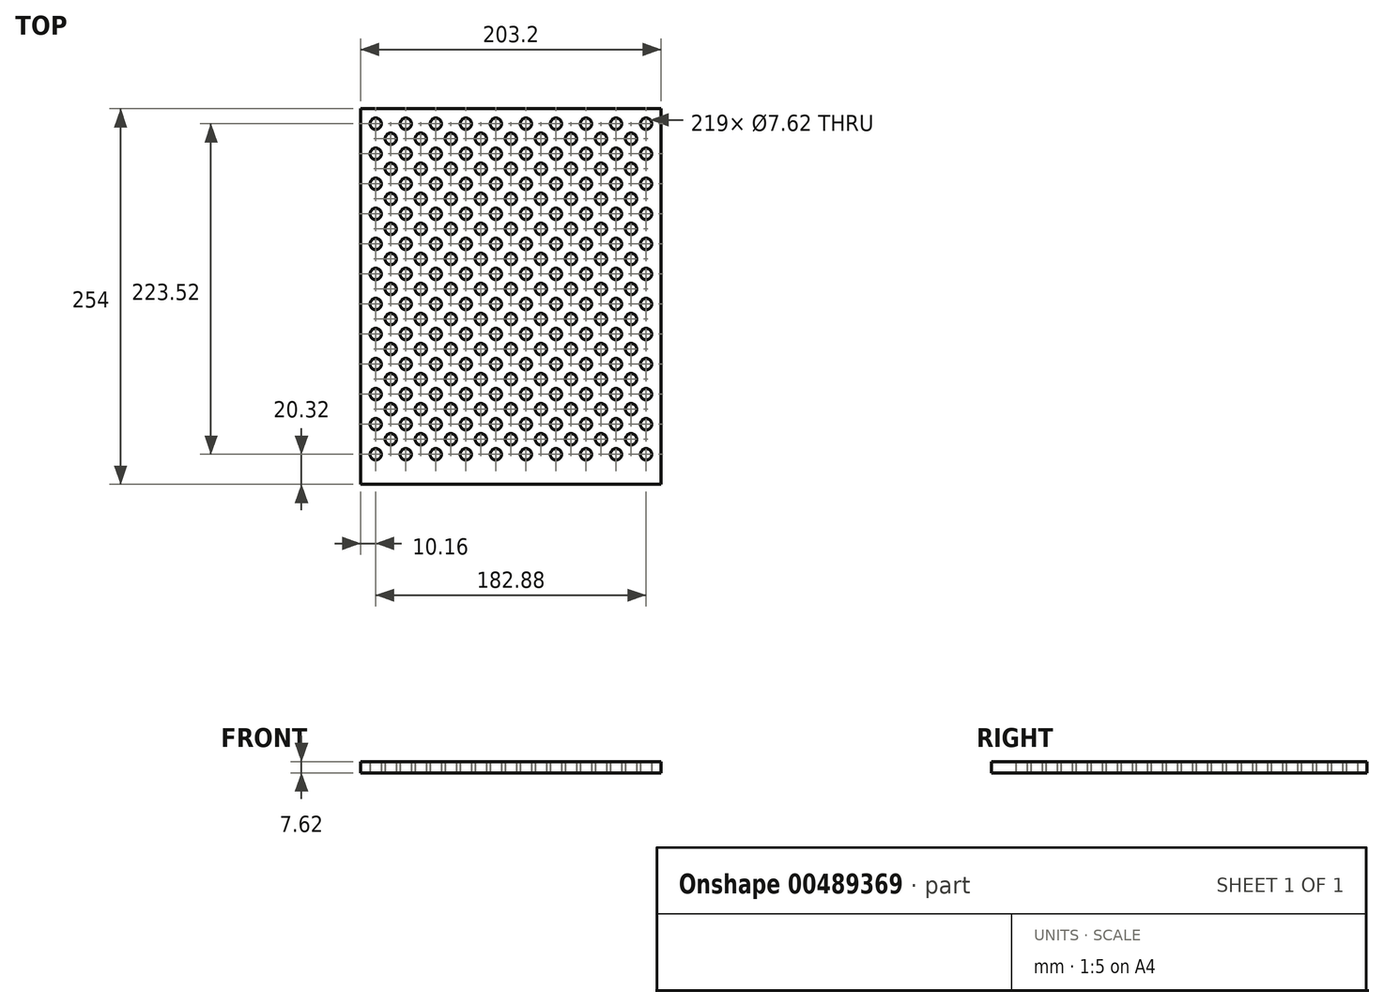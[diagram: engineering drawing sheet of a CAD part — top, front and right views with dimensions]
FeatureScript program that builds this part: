
annotation { "Feature Type Name" : "Feature", "Feature Type Description" : "" }
export const myFeature = defineFeature(function(context is Context, id is Id, definition is map)
    precondition{}
    {
        {
            var Q0;
            Q0=qCreatedBy(makeId("Top.planeOp"),FACE);
            var sketch = newSketch(context, id + "F0", { "sketchPlane" : qUnion([Q0])});
            skLineSegment(sketch, "E0.bottom", {"start": v(-101.6, 127) * mm, "end": v(101.6, 127) * mm});
            skLineSegment(sketch, "E0.top", {"start": v(-101.6, -127) * mm, "end": v(101.6, -127) * mm});
            skLineSegment(sketch, "E0.left", {"start": v(-101.6, 127) * mm, "end": v(-101.6, -127) * mm});
            skLineSegment(sketch, "E0.right", {"start": v(101.6, 127) * mm, "end": v(101.6, -127) * mm});
            skCircle(sketch, "E1", {"center": v(-91.44, 116.84) * mm, "radius": 3.8 * mm});
            skCircle(sketch, "E2", {"center": v(-81.28, 106.68) * mm, "radius": 3.8 * mm});
            skCircle(sketch, "E3", {"center": v(-91.44, 96.52) * mm, "radius": 3.8 * mm});
            skCircle(sketch, "E4", {"center": v(-81.28, 66.04) * mm, "radius": 3.8 * mm});
            skCircle(sketch, "E5", {"center": v(-91.44, 76.2) * mm, "radius": 3.8 * mm});
            skCircle(sketch, "E6", {"center": v(-81.28, 86.36) * mm, "radius": 3.8 * mm});
            skCircle(sketch, "E7", {"center": v(-91.44, 55.88) * mm, "radius": 3.8 * mm});
            skCircle(sketch, "E8", {"center": v(-81.28, 45.72) * mm, "radius": 3.8 * mm});
            skCircle(sketch, "E9", {"center": v(-91.44, 35.56) * mm, "radius": 3.8 * mm});
            skCircle(sketch, "E10", {"center": v(-81.28, 25.4) * mm, "radius": 3.8 * mm});
            skCircle(sketch, "E11", {"center": v(-91.44, 15.24) * mm, "radius": 3.8 * mm});
            skCircle(sketch, "E12", {"center": v(-91.44, -5.08) * mm, "radius": 3.8 * mm});
            skCircle(sketch, "E13", {"center": v(-81.28, 5.08) * mm, "radius": 3.8 * mm});
            skCircle(sketch, "E14", {"center": v(-81.28, -15.24) * mm, "radius": 3.8 * mm});
            skCircle(sketch, "E15", {"center": v(-91.44, -25.4) * mm, "radius": 3.8 * mm});
            skCircle(sketch, "E16", {"center": v(-81.28, -35.56) * mm, "radius": 3.8 * mm});
            skCircle(sketch, "E17", {"center": v(-91.44, -86.36) * mm, "radius": 3.8 * mm});
            skCircle(sketch, "E18", {"center": v(-91.44, -45.72) * mm, "radius": 3.8 * mm});
            skCircle(sketch, "E19", {"center": v(-81.28, -76.2) * mm, "radius": 3.8 * mm});
            skCircle(sketch, "E20", {"center": v(-81.28, -55.88) * mm, "radius": 3.8 * mm});
            skCircle(sketch, "E21", {"center": v(-81.28, -96.52) * mm, "radius": 3.8 * mm});
            skCircle(sketch, "E22", {"center": v(-91.44, -66.04) * mm, "radius": 3.8 * mm});
            skCircle(sketch, "E23", {"center": v(-91.44, -106.68) * mm, "radius": 3.8 * mm});
            skLineSegment(sketch, "E24", {"start": v(-91.44, 116.84) * mm, "end": v(-91.44, -106.68) * mm});
            skLineSegment(sketch, "E25", {"start": v(-81.28, 127) * mm, "end": v(-81.28, -127) * mm, "construction": true});
            skCircle(sketch, "E26.MirrorC", {"center": v(-71.12, 116.84) * mm, "radius": 3.8 * mm});
            skCircle(sketch, "E27.MirrorC", {"center": v(-71.12, 96.52) * mm, "radius": 3.8 * mm});
            skCircle(sketch, "E28.MirrorC", {"center": v(-71.12, 76.2) * mm, "radius": 3.8 * mm});
            skCircle(sketch, "E29.MirrorC", {"center": v(-71.12, 55.88) * mm, "radius": 3.8 * mm});
            skCircle(sketch, "E30.MirrorC", {"center": v(-71.12, 35.56) * mm, "radius": 3.8 * mm});
            skCircle(sketch, "E31.MirrorC", {"center": v(-71.12, 15.24) * mm, "radius": 3.8 * mm});
            skCircle(sketch, "E32.MirrorC", {"center": v(-71.12, -5.08) * mm, "radius": 3.8 * mm});
            skCircle(sketch, "E33.MirrorC", {"center": v(-71.12, -25.4) * mm, "radius": 3.8 * mm});
            skCircle(sketch, "E34.MirrorC", {"center": v(-71.12, -45.72) * mm, "radius": 3.8 * mm});
            skCircle(sketch, "E35.MirrorC", {"center": v(-71.12, -66.04) * mm, "radius": 3.8 * mm});
            skCircle(sketch, "E36.MirrorC", {"center": v(-71.12, -86.36) * mm, "radius": 3.8 * mm});
            skCircle(sketch, "E37.MirrorC", {"center": v(-71.12, -106.68) * mm, "radius": 3.8 * mm});
            skLineSegment(sketch, "E38", {"start": v(-71.12, 127) * mm, "end": v(-71.12, -127) * mm, "construction": true});
            skCircle(sketch, "E39.MirrorC", {"center": v(-60.96, 106.68) * mm, "radius": 3.8 * mm});
            skCircle(sketch, "E40.MirrorC", {"center": v(-60.96, 86.36) * mm, "radius": 3.8 * mm});
            skCircle(sketch, "E41.MirrorC", {"center": v(-60.96, 66.04) * mm, "radius": 3.8 * mm});
            skCircle(sketch, "E42.MirrorC", {"center": v(-60.96, 45.72) * mm, "radius": 3.8 * mm});
            skCircle(sketch, "E43.MirrorC", {"center": v(-60.96, 25.4) * mm, "radius": 3.8 * mm});
            skCircle(sketch, "E44.MirrorC", {"center": v(-60.96, 5.08) * mm, "radius": 3.8 * mm});
            skCircle(sketch, "E45.MirrorC", {"center": v(-60.96, -15.24) * mm, "radius": 3.8 * mm});
            skCircle(sketch, "E46.MirrorC", {"center": v(-60.96, -35.56) * mm, "radius": 3.8 * mm});
            skCircle(sketch, "E47.MirrorC", {"center": v(-60.96, -55.88) * mm, "radius": 3.8 * mm});
            skCircle(sketch, "E48.MirrorC", {"center": v(-60.96, -76.2) * mm, "radius": 3.8 * mm});
            skCircle(sketch, "E49.MirrorC", {"center": v(-60.96, -96.52) * mm, "radius": 3.8 * mm});
            skLineSegment(sketch, "E50", {"start": v(-60.96, 127) * mm, "end": v(-60.96, -127) * mm, "construction": true});
            skCircle(sketch, "E51.MirrorC", {"center": v(-50.8, 116.84) * mm, "radius": 3.8 * mm});
            skCircle(sketch, "E52.MirrorC", {"center": v(-50.8, 96.52) * mm, "radius": 3.8 * mm});
            skCircle(sketch, "E53.MirrorC", {"center": v(-50.8, 76.2) * mm, "radius": 3.8 * mm});
            skCircle(sketch, "E54.MirrorC", {"center": v(-50.8, 55.88) * mm, "radius": 3.8 * mm});
            skCircle(sketch, "E55.MirrorC", {"center": v(-50.8, 35.56) * mm, "radius": 3.8 * mm});
            skCircle(sketch, "E56.MirrorC", {"center": v(-50.8, 15.24) * mm, "radius": 3.8 * mm});
            skCircle(sketch, "E57.MirrorC", {"center": v(-50.8, -5.08) * mm, "radius": 3.8 * mm});
            skCircle(sketch, "E58.MirrorC", {"center": v(-50.8, -25.4) * mm, "radius": 3.8 * mm});
            skCircle(sketch, "E59.MirrorC", {"center": v(-50.8, -45.72) * mm, "radius": 3.8 * mm});
            skCircle(sketch, "E60.MirrorC", {"center": v(-50.8, -66.04) * mm, "radius": 3.8 * mm});
            skCircle(sketch, "E61.MirrorC", {"center": v(-50.8, -86.36) * mm, "radius": 3.8 * mm});
            skCircle(sketch, "E62.MirrorC", {"center": v(-50.8, -106.68) * mm, "radius": 3.8 * mm});
            skLineSegment(sketch, "E63", {"start": v(-50.8, 127) * mm, "end": v(-50.8, -127) * mm, "construction": true});
            skCircle(sketch, "E64.MirrorC", {"center": v(-40.64, -96.52) * mm, "radius": 3.8 * mm});
            skCircle(sketch, "E65.MirrorC", {"center": v(-40.64, -76.2) * mm, "radius": 3.8 * mm});
            skCircle(sketch, "E66.MirrorC", {"center": v(-40.64, -55.88) * mm, "radius": 3.8 * mm});
            skCircle(sketch, "E67.MirrorC", {"center": v(-40.64, -35.56) * mm, "radius": 3.8 * mm});
            skCircle(sketch, "E68.MirrorC", {"center": v(-40.64, 5.08) * mm, "radius": 3.8 * mm});
            skCircle(sketch, "E69.MirrorC", {"center": v(-40.64, 25.4) * mm, "radius": 3.8 * mm});
            skCircle(sketch, "E70.MirrorC", {"center": v(-40.64, 45.72) * mm, "radius": 3.8 * mm});
            skCircle(sketch, "E71.MirrorC", {"center": v(-40.64, 66.04) * mm, "radius": 3.8 * mm});
            skCircle(sketch, "E72.MirrorC", {"center": v(-40.64, 86.36) * mm, "radius": 3.8 * mm});
            skCircle(sketch, "E73.MirrorC", {"center": v(-40.64, 106.68) * mm, "radius": 3.8 * mm});
            skCircle(sketch, "E74.MirrorC", {"center": v(-40.64, -15.24) * mm, "radius": 3.8 * mm});
            skLineSegment(sketch, "E75", {"start": v(-40.64, 127) * mm, "end": v(-40.64, -127) * mm, "construction": true});
            skCircle(sketch, "E76.MirrorC", {"center": v(-30.48, 116.84) * mm, "radius": 3.8 * mm});
            skCircle(sketch, "E77.MirrorC", {"center": v(-30.48, 96.52) * mm, "radius": 3.8 * mm});
            skCircle(sketch, "E78.MirrorC", {"center": v(-30.48, 76.2) * mm, "radius": 3.8 * mm});
            skCircle(sketch, "E79.MirrorC", {"center": v(-30.48, 55.88) * mm, "radius": 3.8 * mm});
            skCircle(sketch, "E80.MirrorC", {"center": v(-30.48, 35.56) * mm, "radius": 3.8 * mm});
            skCircle(sketch, "E81.MirrorC", {"center": v(-30.48, 15.24) * mm, "radius": 3.8 * mm});
            skCircle(sketch, "E82.MirrorC", {"center": v(-30.48, -5.08) * mm, "radius": 3.8 * mm});
            skCircle(sketch, "E83.MirrorC", {"center": v(-30.48, -25.4) * mm, "radius": 3.8 * mm});
            skCircle(sketch, "E84.MirrorC", {"center": v(-30.48, -45.72) * mm, "radius": 3.8 * mm});
            skCircle(sketch, "E85.MirrorC", {"center": v(-30.48, -66.04) * mm, "radius": 3.8 * mm});
            skCircle(sketch, "E86.MirrorC", {"center": v(-30.48, -86.36) * mm, "radius": 3.8 * mm});
            skCircle(sketch, "E87.MirrorC", {"center": v(-30.48, -106.68) * mm, "radius": 3.8 * mm});
            skLineSegment(sketch, "E88", {"start": v(-30.48, 127) * mm, "end": v(-30.48, -127) * mm, "construction": true});
            skCircle(sketch, "E89.MirrorC", {"center": v(-20.32, 106.68) * mm, "radius": 3.8 * mm});
            skCircle(sketch, "E90.MirrorC", {"center": v(-20.32, 86.36) * mm, "radius": 3.8 * mm});
            skCircle(sketch, "E91.MirrorC", {"center": v(-20.32, 45.72) * mm, "radius": 3.8 * mm});
            skCircle(sketch, "E92.MirrorC", {"center": v(-20.32, 5.08) * mm, "radius": 3.8 * mm});
            skCircle(sketch, "E93.MirrorC", {"center": v(-20.32, -35.56) * mm, "radius": 3.8 * mm});
            skCircle(sketch, "E94.MirrorC", {"center": v(-20.32, -15.24) * mm, "radius": 3.8 * mm});
            skCircle(sketch, "E95.MirrorC", {"center": v(-20.32, -55.88) * mm, "radius": 3.8 * mm});
            skCircle(sketch, "E96.MirrorC", {"center": v(-20.32, -76.2) * mm, "radius": 3.8 * mm});
            skCircle(sketch, "E97.MirrorC", {"center": v(-20.32, -96.52) * mm, "radius": 3.8 * mm});
            skCircle(sketch, "E98.MirrorC", {"center": v(-20.32, 25.4) * mm, "radius": 3.8 * mm});
            skCircle(sketch, "E99.MirrorC", {"center": v(-20.32, 66.04) * mm, "radius": 3.8 * mm});
            skLineSegment(sketch, "E100", {"start": v(-20.32, 127) * mm, "end": v(-20.32, -127) * mm, "construction": true});
            skCircle(sketch, "E101.MirrorC", {"center": v(-10.16, 116.84) * mm, "radius": 3.8 * mm});
            skCircle(sketch, "E102.MirrorC", {"center": v(-10.16, 96.52) * mm, "radius": 3.8 * mm});
            skCircle(sketch, "E103.MirrorC", {"center": v(-10.16, 76.2) * mm, "radius": 3.8 * mm});
            skCircle(sketch, "E104.MirrorC", {"center": v(-10.16, 55.88) * mm, "radius": 3.8 * mm});
            skCircle(sketch, "E105.MirrorC", {"center": v(-10.16, 35.56) * mm, "radius": 3.8 * mm});
            skCircle(sketch, "E106.MirrorC", {"center": v(-10.16, 15.24) * mm, "radius": 3.8 * mm});
            skCircle(sketch, "E107.MirrorC", {"center": v(-10.16, -5.08) * mm, "radius": 3.8 * mm});
            skCircle(sketch, "E108.MirrorC", {"center": v(-10.16, -25.4) * mm, "radius": 3.8 * mm});
            skCircle(sketch, "E109.MirrorC", {"center": v(-10.16, -45.72) * mm, "radius": 3.8 * mm});
            skCircle(sketch, "E110.MirrorC", {"center": v(-10.16, -66.04) * mm, "radius": 3.8 * mm});
            skCircle(sketch, "E111.MirrorC", {"center": v(-10.16, -86.36) * mm, "radius": 3.8 * mm});
            skCircle(sketch, "E112.MirrorC", {"center": v(-10.16, -106.68) * mm, "radius": 3.8 * mm});
            skLineSegment(sketch, "E113", {"start": v(-10.16, -127) * mm, "end": v(-10.16, 127) * mm, "construction": true});
            skCircle(sketch, "E114.MirrorC", {"center": v(0, 106.68) * mm, "radius": 3.8 * mm});
            skCircle(sketch, "E115.MirrorC", {"center": v(0, 86.36) * mm, "radius": 3.8 * mm});
            skCircle(sketch, "E116.MirrorC", {"center": v(0, 66.04) * mm, "radius": 3.8 * mm});
            skCircle(sketch, "E117.MirrorC", {"center": v(0, 45.72) * mm, "radius": 3.8 * mm});
            skCircle(sketch, "E118.MirrorC", {"center": v(0, 25.4) * mm, "radius": 3.8 * mm});
            skCircle(sketch, "E119.MirrorC", {"center": v(0, 5.08) * mm, "radius": 3.8 * mm});
            skCircle(sketch, "E120.MirrorC", {"center": v(0, -15.24) * mm, "radius": 3.8 * mm});
            skCircle(sketch, "E121.MirrorC", {"center": v(0, -35.56) * mm, "radius": 3.8 * mm});
            skCircle(sketch, "E122.MirrorC", {"center": v(0, -55.88) * mm, "radius": 3.8 * mm});
            skCircle(sketch, "E123.MirrorC", {"center": v(0, -76.2) * mm, "radius": 3.8 * mm});
            skCircle(sketch, "E124.MirrorC", {"center": v(0, -96.52) * mm, "radius": 3.8 * mm});
            skLineSegment(sketch, "E125", {"start": v(0, 127) * mm, "end": v(0, -127) * mm, "construction": true});
            skCircle(sketch, "E126.MirrorC", {"center": v(10.16, -106.68) * mm, "radius": 3.8 * mm});
            skCircle(sketch, "E127.MirrorC", {"center": v(30.48, -106.68) * mm, "radius": 3.8 * mm});
            skCircle(sketch, "E128.MirrorC", {"center": v(50.8, -106.68) * mm, "radius": 3.8 * mm});
            skCircle(sketch, "E129.MirrorC", {"center": v(71.12, -106.68) * mm, "radius": 3.8 * mm});
            skCircle(sketch, "E130.MirrorC", {"center": v(91.44, -106.68) * mm, "radius": 3.8 * mm});
            skCircle(sketch, "E131.MirrorC", {"center": v(81.28, -96.52) * mm, "radius": 3.8 * mm});
            skCircle(sketch, "E132.MirrorC", {"center": v(60.96, -96.52) * mm, "radius": 3.8 * mm});
            skCircle(sketch, "E133.MirrorC", {"center": v(40.64, -96.52) * mm, "radius": 3.8 * mm});
            skCircle(sketch, "E134.MirrorC", {"center": v(20.32, -96.52) * mm, "radius": 3.8 * mm});
            skCircle(sketch, "E135.MirrorC", {"center": v(10.16, -86.36) * mm, "radius": 3.8 * mm});
            skCircle(sketch, "E136.MirrorC", {"center": v(30.48, -86.36) * mm, "radius": 3.8 * mm});
            skCircle(sketch, "E137.MirrorC", {"center": v(50.8, -86.36) * mm, "radius": 3.8 * mm});
            skCircle(sketch, "E138.MirrorC", {"center": v(71.12, -86.36) * mm, "radius": 3.8 * mm});
            skCircle(sketch, "E139.MirrorC", {"center": v(91.44, -86.36) * mm, "radius": 3.8 * mm});
            skCircle(sketch, "E140.MirrorC", {"center": v(81.28, -76.2) * mm, "radius": 3.8 * mm});
            skCircle(sketch, "E141.MirrorC", {"center": v(60.96, -76.2) * mm, "radius": 3.8 * mm});
            skCircle(sketch, "E142.MirrorC", {"center": v(40.64, -76.2) * mm, "radius": 3.8 * mm});
            skCircle(sketch, "E143.MirrorC", {"center": v(20.32, -76.2) * mm, "radius": 3.8 * mm});
            skCircle(sketch, "E144.MirrorC", {"center": v(10.16, -66.04) * mm, "radius": 3.8 * mm});
            skCircle(sketch, "E145.MirrorC", {"center": v(30.48, -66.04) * mm, "radius": 3.8 * mm});
            skCircle(sketch, "E146.MirrorC", {"center": v(50.8, -66.04) * mm, "radius": 3.8 * mm});
            skCircle(sketch, "E147.MirrorC", {"center": v(71.12, -66.04) * mm, "radius": 3.8 * mm});
            skCircle(sketch, "E148.MirrorC", {"center": v(91.44, -66.04) * mm, "radius": 3.8 * mm});
            skCircle(sketch, "E149.MirrorC", {"center": v(81.28, -55.88) * mm, "radius": 3.8 * mm});
            skCircle(sketch, "E150.MirrorC", {"center": v(60.96, -55.88) * mm, "radius": 3.8 * mm});
            skCircle(sketch, "E151.MirrorC", {"center": v(40.64, -55.88) * mm, "radius": 3.8 * mm});
            skCircle(sketch, "E152.MirrorC", {"center": v(20.32, -55.88) * mm, "radius": 3.8 * mm});
            skCircle(sketch, "E153.MirrorC", {"center": v(10.16, -45.72) * mm, "radius": 3.8 * mm});
            skCircle(sketch, "E154.MirrorC", {"center": v(30.48, -45.72) * mm, "radius": 3.8 * mm});
            skCircle(sketch, "E155.MirrorC", {"center": v(50.8, -45.72) * mm, "radius": 3.8 * mm});
            skCircle(sketch, "E156.MirrorC", {"center": v(71.12, -45.72) * mm, "radius": 3.8 * mm});
            skCircle(sketch, "E157.MirrorC", {"center": v(91.44, -45.72) * mm, "radius": 3.8 * mm});
            skCircle(sketch, "E158.MirrorC", {"center": v(81.28, -35.56) * mm, "radius": 3.8 * mm});
            skCircle(sketch, "E159.MirrorC", {"center": v(60.96, -35.56) * mm, "radius": 3.8 * mm});
            skCircle(sketch, "E160.MirrorC", {"center": v(40.64, -35.56) * mm, "radius": 3.8 * mm});
            skCircle(sketch, "E161.MirrorC", {"center": v(20.32, -35.56) * mm, "radius": 3.8 * mm});
            skCircle(sketch, "E162.MirrorC", {"center": v(10.16, -25.4) * mm, "radius": 3.8 * mm});
            skCircle(sketch, "E163.MirrorC", {"center": v(30.48, -25.4) * mm, "radius": 3.8 * mm});
            skCircle(sketch, "E164.MirrorC", {"center": v(50.8, -25.4) * mm, "radius": 3.8 * mm});
            skCircle(sketch, "E165.MirrorC", {"center": v(71.12, -25.4) * mm, "radius": 3.8 * mm});
            skCircle(sketch, "E166.MirrorC", {"center": v(91.44, -25.4) * mm, "radius": 3.8 * mm});
            skCircle(sketch, "E167.MirrorC", {"center": v(20.32, -15.24) * mm, "radius": 3.8 * mm});
            skCircle(sketch, "E168.MirrorC", {"center": v(40.64, -15.24) * mm, "radius": 3.8 * mm});
            skCircle(sketch, "E169.MirrorC", {"center": v(60.96, -15.24) * mm, "radius": 3.8 * mm});
            skCircle(sketch, "E170.MirrorC", {"center": v(81.28, -15.24) * mm, "radius": 3.8 * mm});
            skCircle(sketch, "E171.MirrorC", {"center": v(91.44, -5.08) * mm, "radius": 3.8 * mm});
            skCircle(sketch, "E172.MirrorC", {"center": v(71.12, -5.08) * mm, "radius": 3.8 * mm});
            skCircle(sketch, "E173.MirrorC", {"center": v(50.8, -5.08) * mm, "radius": 3.8 * mm});
            skCircle(sketch, "E174.MirrorC", {"center": v(30.48, -5.08) * mm, "radius": 3.8 * mm});
            skCircle(sketch, "E175.MirrorC", {"center": v(10.16, -5.08) * mm, "radius": 3.8 * mm});
            skCircle(sketch, "E176.MirrorC", {"center": v(20.32, 5.08) * mm, "radius": 3.8 * mm});
            skCircle(sketch, "E177.MirrorC", {"center": v(40.64, 5.08) * mm, "radius": 3.8 * mm});
            skCircle(sketch, "E178.MirrorC", {"center": v(60.96, 5.08) * mm, "radius": 3.8 * mm});
            skCircle(sketch, "E179.MirrorC", {"center": v(81.28, 5.08) * mm, "radius": 3.8 * mm});
            skCircle(sketch, "E180.MirrorC", {"center": v(91.44, 15.24) * mm, "radius": 3.8 * mm});
            skCircle(sketch, "E181.MirrorC", {"center": v(71.12, 15.24) * mm, "radius": 3.8 * mm});
            skCircle(sketch, "E182.MirrorC", {"center": v(50.8, 15.24) * mm, "radius": 3.8 * mm});
            skCircle(sketch, "E183.MirrorC", {"center": v(30.48, 15.24) * mm, "radius": 3.8 * mm});
            skCircle(sketch, "E184.MirrorC", {"center": v(10.16, 15.24) * mm, "radius": 3.8 * mm});
            skCircle(sketch, "E185.MirrorC", {"center": v(20.32, 25.4) * mm, "radius": 3.8 * mm});
            skCircle(sketch, "E186.MirrorC", {"center": v(40.64, 25.4) * mm, "radius": 3.8 * mm});
            skCircle(sketch, "E187.MirrorC", {"center": v(60.96, 25.4) * mm, "radius": 3.8 * mm});
            skCircle(sketch, "E188.MirrorC", {"center": v(81.28, 25.4) * mm, "radius": 3.8 * mm});
            skCircle(sketch, "E189.MirrorC", {"center": v(91.44, 35.56) * mm, "radius": 3.8 * mm});
            skCircle(sketch, "E190.MirrorC", {"center": v(81.28, 45.72) * mm, "radius": 3.8 * mm});
            skCircle(sketch, "E191.MirrorC", {"center": v(60.96, 45.72) * mm, "radius": 3.8 * mm});
            skCircle(sketch, "E192.MirrorC", {"center": v(40.64, 45.72) * mm, "radius": 3.8 * mm});
            skCircle(sketch, "E193.MirrorC", {"center": v(20.32, 45.72) * mm, "radius": 3.8 * mm});
            skCircle(sketch, "E194.MirrorC", {"center": v(10.16, 55.88) * mm, "radius": 3.8 * mm});
            skCircle(sketch, "E195.MirrorC", {"center": v(30.48, 55.88) * mm, "radius": 3.8 * mm});
            skCircle(sketch, "E196.MirrorC", {"center": v(50.8, 55.88) * mm, "radius": 3.8 * mm});
            skCircle(sketch, "E197.MirrorC", {"center": v(71.12, 55.88) * mm, "radius": 3.8 * mm});
            skCircle(sketch, "E198.MirrorC", {"center": v(91.44, 55.88) * mm, "radius": 3.8 * mm});
            skCircle(sketch, "E199.MirrorC", {"center": v(10.16, 35.56) * mm, "radius": 3.8 * mm});
            skCircle(sketch, "E200.MirrorC", {"center": v(30.48, 35.56) * mm, "radius": 3.8 * mm});
            skCircle(sketch, "E201.MirrorC", {"center": v(50.8, 35.56) * mm, "radius": 3.8 * mm});
            skCircle(sketch, "E202.MirrorC", {"center": v(71.12, 35.56) * mm, "radius": 3.8 * mm});
            skCircle(sketch, "E203.MirrorC", {"center": v(20.32, 66.04) * mm, "radius": 3.8 * mm});
            skCircle(sketch, "E204.MirrorC", {"center": v(40.64, 66.04) * mm, "radius": 3.8 * mm});
            skCircle(sketch, "E205.MirrorC", {"center": v(60.96, 66.04) * mm, "radius": 3.8 * mm});
            skCircle(sketch, "E206.MirrorC", {"center": v(81.28, 66.04) * mm, "radius": 3.8 * mm});
            skCircle(sketch, "E207.MirrorC", {"center": v(91.44, 76.2) * mm, "radius": 3.8 * mm});
            skCircle(sketch, "E208.MirrorC", {"center": v(71.12, 76.2) * mm, "radius": 3.8 * mm});
            skCircle(sketch, "E209.MirrorC", {"center": v(50.8, 76.2) * mm, "radius": 3.8 * mm});
            skCircle(sketch, "E210.MirrorC", {"center": v(30.48, 76.2) * mm, "radius": 3.8 * mm});
            skCircle(sketch, "E211.MirrorC", {"center": v(10.16, 76.2) * mm, "radius": 3.8 * mm});
            skCircle(sketch, "E212.MirrorC", {"center": v(20.32, 86.36) * mm, "radius": 3.8 * mm});
            skCircle(sketch, "E213.MirrorC", {"center": v(40.64, 86.36) * mm, "radius": 3.8 * mm});
            skCircle(sketch, "E214.MirrorC", {"center": v(60.96, 86.36) * mm, "radius": 3.8 * mm});
            skCircle(sketch, "E215.MirrorC", {"center": v(81.28, 86.36) * mm, "radius": 3.8 * mm});
            skCircle(sketch, "E216.MirrorC", {"center": v(91.44, 96.52) * mm, "radius": 3.8 * mm});
            skCircle(sketch, "E217.MirrorC", {"center": v(81.28, 106.68) * mm, "radius": 3.8 * mm});
            skCircle(sketch, "E218.MirrorC", {"center": v(60.96, 106.68) * mm, "radius": 3.8 * mm});
            skCircle(sketch, "E219.MirrorC", {"center": v(40.64, 106.68) * mm, "radius": 3.8 * mm});
            skCircle(sketch, "E220.MirrorC", {"center": v(20.32, 106.68) * mm, "radius": 3.8 * mm});
            skCircle(sketch, "E221.MirrorC", {"center": v(10.16, 116.84) * mm, "radius": 3.8 * mm});
            skCircle(sketch, "E222.MirrorC", {"center": v(30.48, 116.84) * mm, "radius": 3.8 * mm});
            skCircle(sketch, "E223.MirrorC", {"center": v(50.8, 116.84) * mm, "radius": 3.8 * mm});
            skCircle(sketch, "E224.MirrorC", {"center": v(71.12, 116.84) * mm, "radius": 3.8 * mm});
            skCircle(sketch, "E225.MirrorC", {"center": v(91.44, 116.84) * mm, "radius": 3.8 * mm});
            skCircle(sketch, "E226.MirrorC", {"center": v(30.48, 96.52) * mm, "radius": 3.8 * mm});
            skCircle(sketch, "E227.MirrorC", {"center": v(50.8, 96.52) * mm, "radius": 3.8 * mm});
            skCircle(sketch, "E228.MirrorC", {"center": v(71.12, 96.52) * mm, "radius": 3.8 * mm});
            skCircle(sketch, "E229.MirrorC", {"center": v(10.16, 96.52) * mm, "radius": 3.8 * mm});
            skSolve(sketch);
        }
        {
            var Q0;
            Q0=makeQuery(id+"F0.imprint","IMPRINT",FACE,{"disambiguationData":[TD([[makeQuery(id+"F0.imprint","IMPRINT",EDGE,{"derivedFrom":sQuery(id+"F0.wireOp",EDGE,"E0.bottom")}),-1.0]])]});
            extrude(context, id + "F1", {"entities" : qUnion([Q0]), "depth" : 7.62 * mm});
        }
    });
